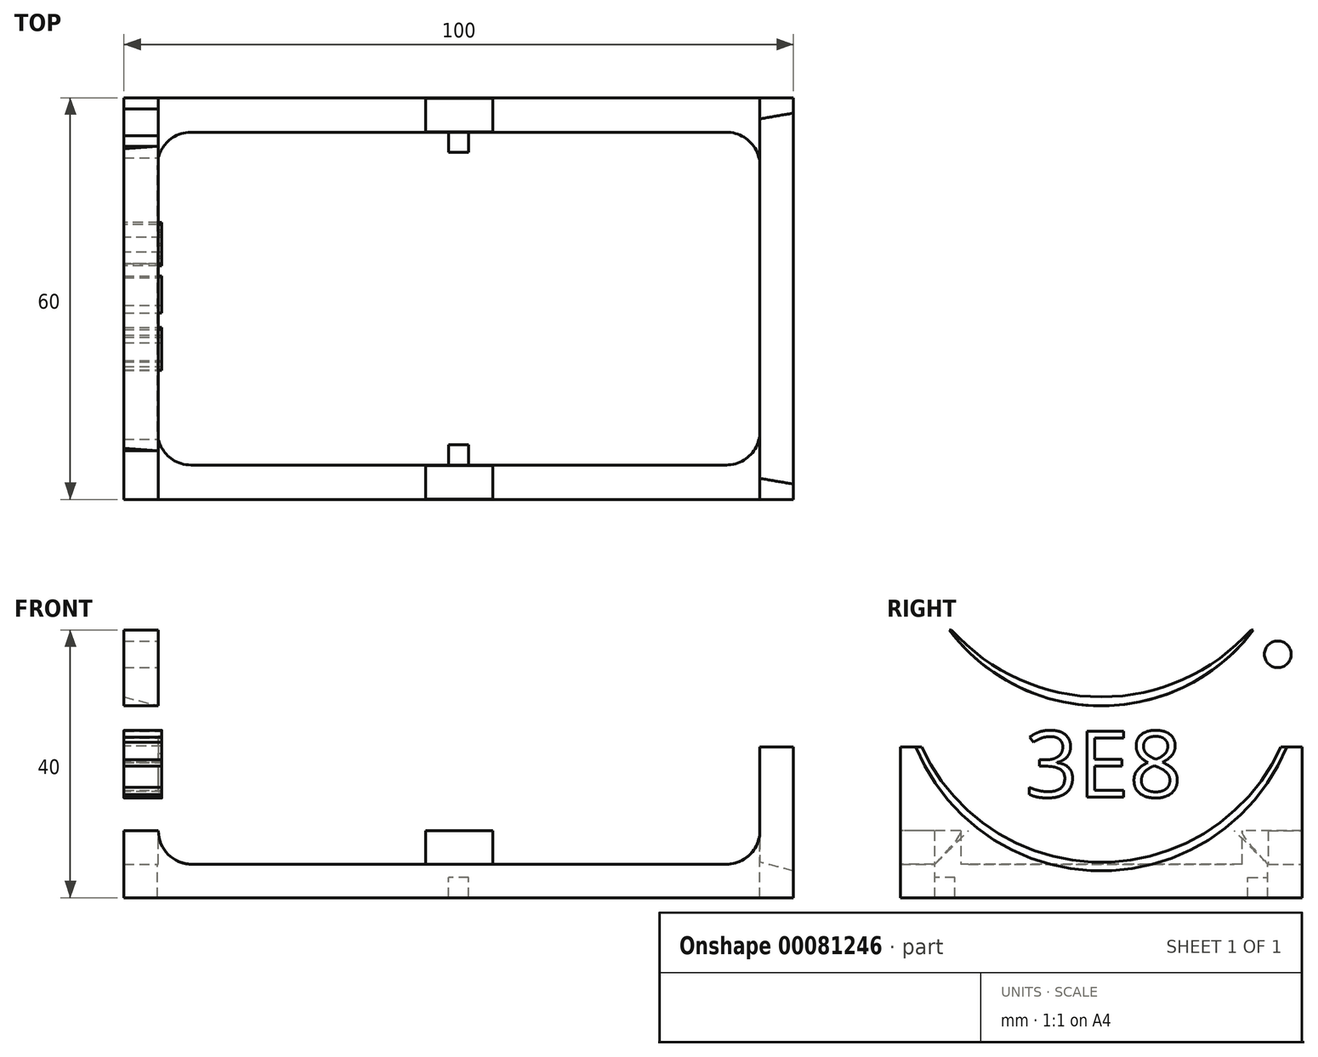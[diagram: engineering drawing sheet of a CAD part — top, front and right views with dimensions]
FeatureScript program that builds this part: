
annotation { "Feature Type Name" : "Feature", "Feature Type Description" : "" }
export const myFeature = defineFeature(function(context is Context, id is Id, definition is map)
    precondition{}
    {
        {
            var Q0;
            Q0=qCreatedBy(makeId("Top.planeOp"),FACE);
            var sketch = newSketch(context, id + "F0", { "sketchPlane" : qUnion([Q0])});
            skLineSegment(sketch, "E0.bottom", {"start": v(50, -30) * mm, "end": v(-50, -30) * mm});
            skLineSegment(sketch, "E0.top", {"start": v(50, 30) * mm, "end": v(-50, 30) * mm});
            skLineSegment(sketch, "E0.left", {"start": v(50, -30) * mm, "end": v(50, 30) * mm});
            skLineSegment(sketch, "E0.right", {"start": v(-50, -30) * mm, "end": v(-50, 30) * mm});
            skPoint(sketch, "E0.middle", {"position": v(0, 0) * mm});
            skSolve(sketch);
        }
        {
            var Q0;
            Q0 = qSketchRegion(id + "F0", true);
            extrude(context, id + "F1", {"entities" : qUnion([Q0]), "depth" : 40 * mm});
        }
        {
            var Q0;
            Q0=makeQuery(id+"F1.opExtrude","SWEPT_FACE",FACE,{"disambiguationData":[OSD([sQuery(id+"F0.wireOp",EDGE,"E0.left")])]});
            var sketch = newSketch(context, id + "F2", { "sketchPlane" : qUnion([Q0])});
            skArc(sketch, "E1", {"start": v(-29.4, 40) * mm, "mid": v(0, 4) * mm, "end": v(29.4, 40) * mm});
            skLineSegment(sketch, "E2", {"start": v(0, 4) * mm, "end": v(0, 0) * mm, "construction": true});
            skLineSegment(sketch, "E3", {"start": v(29.4, 40) * mm, "end": v(-29.4, 40) * mm});
            skSolve(sketch);
        }
        {
            var Q0;
            Q0=makeQuery(id+"F1.opExtrude","SWEPT_FACE",FACE,{"disambiguationData":[OSD([sQuery(id+"F0.wireOp",EDGE,"E0.right")])]});
            var sketch = newSketch(context, id + "F3", { "sketchPlane" : qUnion([Q0])});
            skArc(sketch, "E4", {"start": v(-22.36, 40) * mm, "mid": v(0, 30) * mm, "end": v(22.36, 40) * mm});
            skPoint(sketch, "E5.endSnap0", {"position": v(0, 30) * mm});
            skLineSegment(sketch, "E6", {"start": v(0, 30) * mm, "end": v(0, 0) * mm, "construction": true});
            skLineSegment(sketch, "E7", {"start": v(-22.36, 40) * mm, "end": v(22.36, 40) * mm});
            skSolve(sketch);
        }
        {
            var Q1;
            Q1=makeQuery(id+"F3.imprint","IMPRINT",FACE,{"disambiguationData":[TD([[makeQuery(id+"F3.imprint","IMPRINT",EDGE,{"derivedFrom":sQuery(id+"F3.wireOp",EDGE,"E4")}),1.0]])]});
            var Q2;
            Q2=makeQuery(id+"F2.imprint","IMPRINT",FACE,{"disambiguationData":[TD([[makeQuery(id+"F2.imprint","IMPRINT",EDGE,{"derivedFrom":sQuery(id+"F2.wireOp",EDGE,"E1")}),1.0]])]});
            loft(context, id + "F4", {"operationType" : NewBodyOperationType.REMOVE, "sheetProfilesArray" : [{ "sheetProfileEntities" : qUnion([Q1]) }, { "sheetProfileEntities" : qUnion([Q2]) }]});
        }
        {
            var Q0;
            Q0=makeQuery(id+"F1.opExtrude","SWEPT_FACE",FACE,{"disambiguationData":[OSD([sQuery(id+"F0.wireOp",EDGE,"E0.top")])]});
            var sketch = newSketch(context, id + "F5", { "sketchPlane" : qUnion([Q0])});
            skLineSegment(sketch, "E8", {"start": v(-50, 40) * mm, "end": v(-45, 40) * mm, "construction": true});
            skLineSegment(sketch, "E9.bottom", {"start": v(-45, 40) * mm, "end": v(44.86, 40) * mm});
            skLineSegment(sketch, "E9.top", {"start": v(-45, 5) * mm, "end": v(44.86, 5) * mm});
            skLineSegment(sketch, "E9.left", {"start": v(-45, 40) * mm, "end": v(-45, 5) * mm});
            skLineSegment(sketch, "E9.right", {"start": v(44.86, 40) * mm, "end": v(44.86, 5) * mm});
            skLineSegment(sketch, "E10", {"start": v(0, 5) * mm, "end": v(0, 0) * mm, "construction": true});
            skSolve(sketch);
        }
        {
            var Q0;
            Q0 = qSketchRegion(id + "F5", true);
            extrude(context, id + "F6", {"entities" : qUnion([Q0]), "operationType" : NewBodyOperationType.REMOVE, "endBound" : BoundingType.THROUGH_ALL, "oppositeDirection" : true, "depth" : 25 * mm});
        }
        {
            var Q0;
            Q0=makeQuery(id+"F6.boolean.opBoolean","COPY",FACE,{"derivedFrom":makeQuery(id+"F6.opExtrude","SWEPT_FACE",FACE,{"disambiguationData":[OSD([sQuery(id+"F5.wireOp",EDGE,"E9.top")])]})});
            var sketch = newSketch(context, id + "F7", { "sketchPlane" : qUnion([Q0])});
            skLineSegment(sketch, "E11.bottom", {"start": v(45, -24.86) * mm, "end": v(-45, -24.86) * mm});
            skLineSegment(sketch, "E11.top", {"start": v(45, 24.86) * mm, "end": v(-45, 24.86) * mm});
            skLineSegment(sketch, "E11.left", {"start": v(45, -24.86) * mm, "end": v(45, 24.86) * mm});
            skLineSegment(sketch, "E11.right", {"start": v(-45, -24.86) * mm, "end": v(-45, 24.86) * mm});
            skPoint(sketch, "E11.middle", {"position": v(0, 0) * mm});
            skLineSegment(sketch, "E12.0", {"start": v(-44.86, 30) * mm, "end": v(-50, 30) * mm, "construction": true});
            skLineSegment(sketch, "E13", {"start": v(0, 24.86) * mm, "end": v(0, 30) * mm, "construction": true});
            skSolve(sketch);
        }
        {
            var Q0;
            Q0 = qSketchRegion(id + "F7", true);
            extrude(context, id + "F8", {"entities" : qUnion([Q0]), "operationType" : NewBodyOperationType.REMOVE, "endBound" : BoundingType.THROUGH_ALL, "oppositeDirection" : true, "depth" : 25 * mm});
        }
        {
            var Q0;
            Q0=makeQuery(id+"F1.opExtrude","SWEPT_FACE",FACE,{"disambiguationData":[OSD([sQuery(id+"F0.wireOp",EDGE,"E0.bottom")])]});
            var sketch = newSketch(context, id + "F9", { "sketchPlane" : qUnion([Q0])});
            skPoint(sketch, "E14.oppositeSnap0", {"position": v(45, 22.5) * mm});
            skLineSegment(sketch, "E14.bottom", {"start": v(45, 40) * mm, "end": v(50, 40) * mm});
            skLineSegment(sketch, "E14.top", {"start": v(45, 22.5) * mm, "end": v(50, 22.5) * mm});
            skLineSegment(sketch, "E14.left", {"start": v(45, 40) * mm, "end": v(45, 22.5) * mm});
            skLineSegment(sketch, "E14.right", {"start": v(50, 40) * mm, "end": v(50, 22.5) * mm});
            skSolve(sketch);
        }
        {
            var Q0;
            Q0 = qSketchRegion(id + "F9", true);
            extrude(context, id + "F10", {"entities" : qUnion([Q0]), "operationType" : NewBodyOperationType.REMOVE, "endBound" : BoundingType.THROUGH_ALL, "oppositeDirection" : true, "depth" : 25 * mm});
        }
        {
            var Q0;
            Q0=makeQuery(id+"F8.boolean.opBoolean","SPLIT",FACE,{"disambiguationData":[TD([makeQuery(id+"F1.opExtrude","SWEPT_FACE",FACE,{"disambiguationData":[OSD([sQuery(id+"F0.wireOp",EDGE,"E0.bottom")])]})])],"derivedFrom":makeQuery(id+"F6.boolean.opBoolean","COPY",FACE,{"derivedFrom":makeQuery(id+"F6.opExtrude","SWEPT_FACE",FACE,{"disambiguationData":[OSD([sQuery(id+"F5.wireOp",EDGE,"E9.top")])]})})});
            var sketch = newSketch(context, id + "F11", { "sketchPlane" : qUnion([Q0])});
            skLineSegment(sketch, "E15", {"start": v(-44.86, -30) * mm, "end": v(45, -24.86) * mm, "construction": true});
            skLineSegment(sketch, "E16.bottom", {"start": v(-4.93, -24.93) * mm, "end": v(5.07, -24.93) * mm});
            skLineSegment(sketch, "E16.top", {"start": v(-4.93, -29.93) * mm, "end": v(5.07, -29.93) * mm});
            skLineSegment(sketch, "E16.left", {"start": v(-4.93, -24.93) * mm, "end": v(-4.93, -29.93) * mm});
            skLineSegment(sketch, "E16.right", {"start": v(5.07, -24.93) * mm, "end": v(5.07, -29.93) * mm});
            skPoint(sketch, "E16.middle", {"position": v(0.07, -27.43) * mm});
            skLineSegment(sketch, "E17", {"start": v(0, 0) * mm, "end": v(-10, 0) * mm, "construction": true});
            skLineSegment(sketch, "E18.MirrorCS", {"start": v(-4.93, 24.93) * mm, "end": v(5.07, 24.93) * mm});
            skLineSegment(sketch, "E19.MirrorCS", {"start": v(-4.93, 24.93) * mm, "end": v(-4.93, 29.93) * mm});
            skLineSegment(sketch, "E20.MirrorCS", {"start": v(-4.93, 29.93) * mm, "end": v(5.07, 29.93) * mm});
            skLineSegment(sketch, "E21.MirrorCS", {"start": v(5.07, 24.93) * mm, "end": v(5.07, 29.93) * mm});
            skSolve(sketch);
        }
        {
            var Q0;
            {var subQ0=sQuery(id+"F7.wireOp",EDGE,"E11.bottom");var subQ1=sQuery(id+"F5.wireOp",EDGE,"E9.right");var subQ2=sQuery(id+"F5.wireOp",EDGE,"E9.top");Q0=makeQuery(id+"F8.boolean.opBoolean","SPLIT",EDGE,{"disambiguationData":[TD([makeQuery(id+"F1.opExtrude","SWEPT_FACE",FACE,{"disambiguationData":[OSD([sQuery(id+"F0.wireOp",EDGE,"E0.bottom")])]}),makeQuery(id+"F6.boolean.opBoolean","COPY",FACE,{"derivedFrom":makeQuery(id+"F6.opExtrude","SWEPT_FACE",FACE,{"disambiguationData":[OSD([subQ2])]})}),makeQuery(id+"F6.boolean.opBoolean","COPY",FACE,{"derivedFrom":makeQuery(id+"F6.opExtrude","SWEPT_FACE",FACE,{"disambiguationData":[OSD([subQ1])]})}),makeQuery(id+"F8.opExtrude","SWEPT_FACE",FACE,{"disambiguationData":[OSD([subQ0])]}),makeQuery(id+"F8.opExtrude","CAP_FACE",FACE,{"disambiguationData":[OSD([subQ0,sQuery(id+"F7.wireOp",EDGE,"E11.top"),sQuery(id+"F7.wireOp",EDGE,"E11.left"),sQuery(id+"F7.wireOp",EDGE,"E11.right")])],"isStart":true})])],"derivedFrom":makeQuery(id+"F6.boolean.opBoolean","COPY",EDGE,{"derivedFrom":makeQuery(id+"F6.opExtrude","SWEPT_EDGE",EDGE,{"disambiguationData":[OSD([subQ2,subQ1])]})})});}
            var Q1;
            {var subQ0=sQuery(id+"F7.wireOp",EDGE,"E11.top");var subQ1=sQuery(id+"F5.wireOp",EDGE,"E9.right");var subQ2=sQuery(id+"F5.wireOp",EDGE,"E9.top");Q1=makeQuery(id+"F8.boolean.opBoolean","SPLIT",EDGE,{"disambiguationData":[TD([makeQuery(id+"F1.opExtrude","SWEPT_FACE",FACE,{"disambiguationData":[OSD([sQuery(id+"F0.wireOp",EDGE,"E0.top")])]}),makeQuery(id+"F6.boolean.opBoolean","COPY",FACE,{"derivedFrom":makeQuery(id+"F6.opExtrude","SWEPT_FACE",FACE,{"disambiguationData":[OSD([subQ2])]})}),makeQuery(id+"F6.boolean.opBoolean","COPY",FACE,{"derivedFrom":makeQuery(id+"F6.opExtrude","SWEPT_FACE",FACE,{"disambiguationData":[OSD([subQ1])]})}),makeQuery(id+"F8.opExtrude","CAP_FACE",FACE,{"disambiguationData":[OSD([sQuery(id+"F7.wireOp",EDGE,"E11.bottom"),subQ0,sQuery(id+"F7.wireOp",EDGE,"E11.left"),sQuery(id+"F7.wireOp",EDGE,"E11.right")])],"isStart":true}),makeQuery(id+"F8.opExtrude","SWEPT_FACE",FACE,{"disambiguationData":[OSD([subQ0])]})])],"derivedFrom":makeQuery(id+"F6.boolean.opBoolean","COPY",EDGE,{"derivedFrom":makeQuery(id+"F6.opExtrude","SWEPT_EDGE",EDGE,{"disambiguationData":[OSD([subQ2,subQ1])]})})});}
            var Q2;
            {var subQ0=sQuery(id+"F5.wireOp",EDGE,"E9.left");var subQ1=sQuery(id+"F5.wireOp",EDGE,"E9.top");Q2=makeQuery(id+"F8.boolean.opBoolean","SPLIT",EDGE,{"disambiguationData":[TD([makeQuery(id+"F1.opExtrude","SWEPT_FACE",FACE,{"disambiguationData":[OSD([sQuery(id+"F0.wireOp",EDGE,"E0.bottom")])]})])],"derivedFrom":makeQuery(id+"F6.boolean.opBoolean","COPY",EDGE,{"derivedFrom":makeQuery(id+"F6.opExtrude","SWEPT_EDGE",EDGE,{"disambiguationData":[OSD([subQ1,subQ0])]})})});}
            var Q3;
            {var subQ0=sQuery(id+"F5.wireOp",EDGE,"E9.left");var subQ1=sQuery(id+"F5.wireOp",EDGE,"E9.top");Q3=makeQuery(id+"F8.boolean.opBoolean","SPLIT",EDGE,{"disambiguationData":[TD([makeQuery(id+"F1.opExtrude","SWEPT_FACE",FACE,{"disambiguationData":[OSD([sQuery(id+"F0.wireOp",EDGE,"E0.top")])]})])],"derivedFrom":makeQuery(id+"F6.boolean.opBoolean","COPY",EDGE,{"derivedFrom":makeQuery(id+"F6.opExtrude","SWEPT_EDGE",EDGE,{"disambiguationData":[OSD([subQ1,subQ0])]})})});}
            var Q4;
            Q4=makeQuery(id+"F8.boolean.opBoolean","COPY",EDGE,{"derivedFrom":makeQuery(id+"F8.opExtrude","SWEPT_EDGE",EDGE,{"disambiguationData":[OSD([sQuery(id+"F5.wireOp",EDGE,"E9.top"),sQuery(id+"F5.wireOp",EDGE,"E9.left"),sQuery(id+"F7.wireOp",EDGE,"E11.bottom"),sQuery(id+"F7.wireOp",EDGE,"E11.left")])]})});
            var Q5;
            Q5=makeQuery(id+"F8.boolean.opBoolean","COPY",EDGE,{"derivedFrom":makeQuery(id+"F8.opExtrude","SWEPT_EDGE",EDGE,{"disambiguationData":[OSD([sQuery(id+"F5.wireOp",EDGE,"E9.top"),sQuery(id+"F5.wireOp",EDGE,"E9.left"),sQuery(id+"F7.wireOp",EDGE,"E11.top"),sQuery(id+"F7.wireOp",EDGE,"E11.left")])]})});
            fillet(context, id + "F12", {"entities" : qUnion([Q0, Q1, Q2, Q3, Q4, Q5]), "radius" : 5 * mm, "tangentPropagation" : true, "allowEdgeOverflow" : false});
        }
        {
            var Q0;
            Q0=makeQuery(id+"F8.boolean.opBoolean","COPY",EDGE,{"derivedFrom":makeQuery(id+"F8.opExtrude","SWEPT_EDGE",EDGE,{"disambiguationData":[OSD([sQuery(id+"F7.wireOp",EDGE,"E11.top"),sQuery(id+"F7.wireOp",EDGE,"E11.right")])]})});
            var Q1;
            Q1=makeQuery(id+"F8.boolean.opBoolean","COPY",EDGE,{"derivedFrom":makeQuery(id+"F8.opExtrude","SWEPT_EDGE",EDGE,{"disambiguationData":[OSD([sQuery(id+"F7.wireOp",EDGE,"E11.bottom"),sQuery(id+"F7.wireOp",EDGE,"E11.right")])]})});
            fillet(context, id + "F13", {"entities" : qUnion([Q0, Q1]), "radius" : 5 * mm, "tangentPropagation" : true, "allowEdgeOverflow" : false});
        }
        {
            var Q0;
            Q0 = qSketchRegion(id + "F11", true);
            extrude(context, id + "F14", {"entities" : qUnion([Q0]), "operationType" : NewBodyOperationType.ADD, "depth" : 5 * mm});
        }
        {
            var Q0;
            Q0=makeQuery(id+"F8.boolean.opBoolean","COPY",FACE,{"derivedFrom":makeQuery(id+"F8.opExtrude","SWEPT_FACE",FACE,{"disambiguationData":[OSD([sQuery(id+"F7.wireOp",EDGE,"E11.bottom")])]})});
            var sketch = newSketch(context, id + "F15", { "sketchPlane" : qUnion([Q0])});
            skLineSegment(sketch, "E22.bottom", {"start": v(-1.5, 0) * mm, "end": v(1.5, 0) * mm});
            skLineSegment(sketch, "E22.top", {"start": v(-1.5, 3) * mm, "end": v(1.5, 3) * mm});
            skLineSegment(sketch, "E22.left", {"start": v(-1.5, 0) * mm, "end": v(-1.5, 3) * mm});
            skLineSegment(sketch, "E22.right", {"start": v(1.5, 0) * mm, "end": v(1.5, 3) * mm});
            skPoint(sketch, "E23", {"position": v(0, 0) * mm});
            skSolve(sketch);
        }
        {
            var Q0;
            Q0 = qSketchRegion(id + "F15", true);
            extrude(context, id + "F16", {"entities" : qUnion([Q0]), "operationType" : NewBodyOperationType.ADD, "depth" : 3 * mm});
        }
        {
            var Q0;
            Q0=makeQuery(id+"F8.boolean.opBoolean","COPY",FACE,{"derivedFrom":makeQuery(id+"F8.opExtrude","SWEPT_FACE",FACE,{"disambiguationData":[OSD([sQuery(id+"F7.wireOp",EDGE,"E11.top")])]})});
            var sketch = newSketch(context, id + "F17", { "sketchPlane" : qUnion([Q0])});
            skLineSegment(sketch, "E24.bottom", {"start": v(1.5, 0) * mm, "end": v(-1.5, 0) * mm});
            skLineSegment(sketch, "E24.top", {"start": v(1.5, 3) * mm, "end": v(-1.5, 3) * mm});
            skLineSegment(sketch, "E24.left", {"start": v(1.5, 0) * mm, "end": v(1.5, 3) * mm});
            skLineSegment(sketch, "E24.right", {"start": v(-1.5, 0) * mm, "end": v(-1.5, 3) * mm});
            skPoint(sketch, "E25", {"position": v(0, 0) * mm});
            skSolve(sketch);
        }
        {
            var Q0;
            Q0 = qSketchRegion(id + "F17", true);
            extrude(context, id + "F18", {"entities" : qUnion([Q0]), "operationType" : NewBodyOperationType.ADD, "depth" : 3 * mm});
        }
        {
            var Q0;
            Q0=makeQuery(id+"F6.boolean.opBoolean","COPY",FACE,{"derivedFrom":makeQuery(id+"F6.opExtrude","SWEPT_FACE",FACE,{"disambiguationData":[OSD([sQuery(id+"F5.wireOp",EDGE,"E9.right")])]})});
            var sketch = newSketch(context, id + "F19", { "sketchPlane" : qUnion([Q0])});
            skText(sketch, "E26", { "text": "3E8", "fontName": "OpenSans-Regular.ttf"});
            skPoint(sketch, "E27.0", {"position": v(-30, 0) * mm});
            skPoint(sketch, "E28.0", {"position": v(30, 40) * mm});
            skLineSegment(sketch, "E29", {"start": v(30, 40) * mm, "end": v(-30, 0) * mm, "construction": true});
            skPoint(sketch, "E30", {"position": v(0, 20) * mm});
            skLineSegment(sketch, "E31", {"start": v(-26.36, 40) * mm, "end": v(-26.36, 36.36) * mm, "construction": true});
            skLineSegment(sketch, "E32", {"start": v(-26.36, 36.36) * mm, "end": v(-30, 36.36) * mm, "construction": true});
            skCircle(sketch, "E33", {"center": v(-26.36, 36.36) * mm, "radius": 2 * mm});
            skCircle(sketch, "E34.MirrorC", {"center": v(26.36, 36.36) * mm, "radius": 2 * mm});
            const initialGuessF19  = {"E26": [-0.01137, 0.01503, 1, 0, 0.00993]};
            skSetInitialGuess(sketch, initialGuessF19);
            skSolve(sketch);
        }
        {
            var Q0;
            Q0=makeQuery(id+"F19.imprint","IMPRINT",FACE,{"disambiguationData":[TD([[makeQuery(id+"F19.imprint","IMPRINT",EDGE,{"derivedFrom":sQuery(id+"F19.wireOp",EDGE,"E26.sketch_text.stroke-0")}),-1.0]])]});
            var Q1;
            Q1=makeQuery(id+"F19.imprint","IMPRINT",FACE,{"disambiguationData":[TD([[makeQuery(id+"F19.imprint","IMPRINT",EDGE,{"derivedFrom":sQuery(id+"F19.wireOp",EDGE,"E26.sketch_text.stroke-28")}),-1.0]])]});
            var Q2;
            Q2=makeQuery(id+"F19.imprint","IMPRINT",FACE,{"disambiguationData":[TD([[makeQuery(id+"F19.imprint","IMPRINT",EDGE,{"derivedFrom":sQuery(id+"F19.wireOp",EDGE,"E26.sketch_text.stroke-40")}),-1.0]])]});
            extrude(context, id + "F20", {"entities" : qUnion([Q0, Q1, Q2]), "operationType" : NewBodyOperationType.ADD, "depth" : .5 * mm});
        }
        {
            var Q0;
            {var subQ0=sQuery(id+"F0.wireOp",EDGE,"E0.bottom");var subQ1=sQuery(id+"F0.wireOp",EDGE,"E0.right");Q0=makeQuery(id+"F6.boolean.opBoolean","SPLIT",EDGE,{"disambiguationData":[TD([makeQuery(id+"F1.opExtrude","SWEPT_FACE",FACE,{"disambiguationData":[OSD([subQ1])]})])],"derivedFrom":makeQuery(id+"F1.opExtrude","CAP_EDGE",EDGE,{"disambiguationData":[OSD([subQ0])],"isStart":false})});}
            var Q1;
            {var subQ0=sQuery(id+"F0.wireOp",EDGE,"E0.right");var subQ1=sQuery(id+"F0.wireOp",EDGE,"E0.top");Q1=makeQuery(id+"F6.boolean.opBoolean","SPLIT",EDGE,{"disambiguationData":[TD([makeQuery(id+"F1.opExtrude","SWEPT_FACE",FACE,{"disambiguationData":[OSD([subQ0])]})])],"derivedFrom":makeQuery(id+"F1.opExtrude","CAP_EDGE",EDGE,{"disambiguationData":[OSD([subQ1])],"isStart":false})});}
            fillet(context, id + "F21", {"entities" : qUnion([Q0, Q1]), "radius" : 5 * mm, "tangentPropagation" : true, "allowEdgeOverflow" : false});
        }
        {
            var Q0;
            Q0=makeQuery(id+"F19.imprint","IMPRINT",FACE,{"disambiguationData":[TD([[makeQuery(id+"F19.imprint","IMPRINT",EDGE,{"derivedFrom":sQuery(id+"F19.wireOp",EDGE,"E33")}),1.0]])]});
            var Q1;
            Q1=makeQuery(id+"F19.imprint","IMPRINT",FACE,{"disambiguationData":[TD([[makeQuery(id+"F19.imprint","IMPRINT",EDGE,{"derivedFrom":sQuery(id+"F19.wireOp",EDGE,"E34.MirrorC")}),-1.0]])]});
            extrude(context, id + "F22", {"entities" : qUnion([Q0, Q1]), "operationType" : NewBodyOperationType.REMOVE, "endBound" : BoundingType.THROUGH_ALL, "oppositeDirection" : true, "depth" : 25 * mm});
        }
    });
